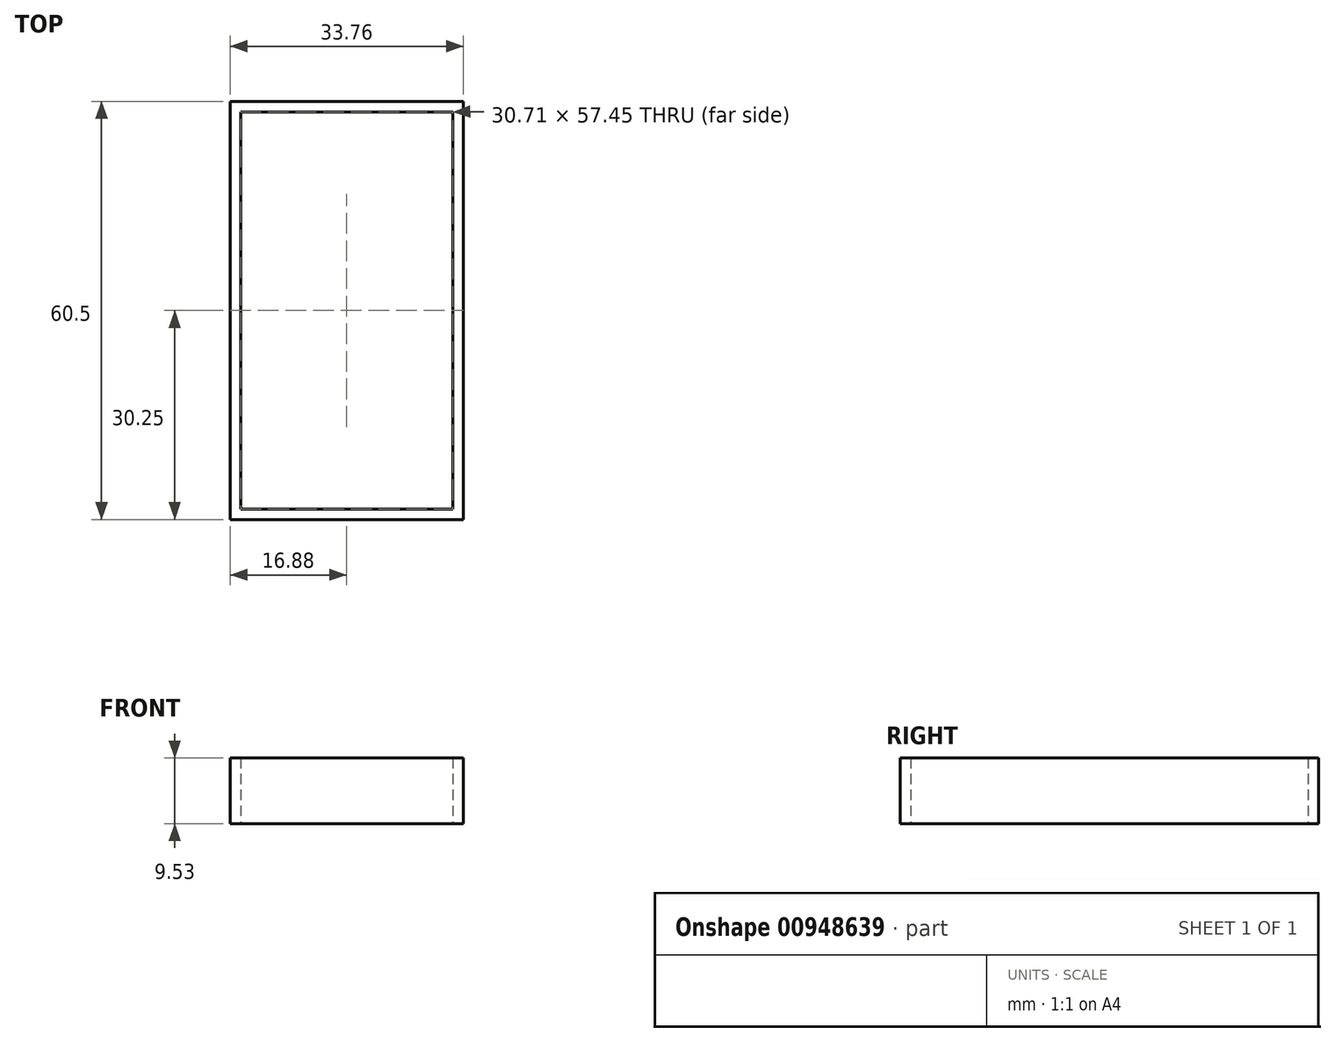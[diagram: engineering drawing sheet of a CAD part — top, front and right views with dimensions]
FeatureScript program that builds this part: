
annotation { "Feature Type Name" : "Feature", "Feature Type Description" : "" }
export const myFeature = defineFeature(function(context is Context, id is Id, definition is map)
    precondition{}
    {
        {
            var Q0;
            Q0=qCreatedBy(makeId("Top.planeOp"),FACE);
            var sketch = newSketch(context, id + "F0", { "sketchPlane" : qUnion([Q0])});
            skLineSegment(sketch, "E0.bottom", {"start": v(-15.35, 28.73) * mm, "end": v(15.35, 28.73) * mm});
            skLineSegment(sketch, "E0.top", {"start": v(-15.35, -28.73) * mm, "end": v(15.35, -28.73) * mm});
            skLineSegment(sketch, "E0.left", {"start": v(-15.35, 28.73) * mm, "end": v(-15.35, -28.73) * mm});
            skLineSegment(sketch, "E0.right", {"start": v(15.35, 28.73) * mm, "end": v(15.35, -28.73) * mm});
            skPoint(sketch, "E0.middle", {"position": v(0, 0) * mm});
            skLineSegment(sketch, "E1.bottom", {"start": v(-16.88, 30.25) * mm, "end": v(16.88, 30.25) * mm});
            skLineSegment(sketch, "E1.top", {"start": v(-16.88, -30.25) * mm, "end": v(16.88, -30.25) * mm});
            skLineSegment(sketch, "E1.left", {"start": v(-16.88, 30.25) * mm, "end": v(-16.88, -30.25) * mm});
            skLineSegment(sketch, "E1.right", {"start": v(16.88, 30.25) * mm, "end": v(16.88, -30.25) * mm});
            skSolve(sketch);
        }
        {
            var Q0;
            Q0=makeQuery(id+"F0.imprint","IMPRINT",FACE,{"disambiguationData":[TD([[makeQuery(id+"F0.imprint","IMPRINT",EDGE,{"derivedFrom":sQuery(id+"F0.wireOp",EDGE,"E0.bottom")}),1.0]])]});
            extrude(context, id + "F1", {"entities" : qUnion([Q0]), "depth" : 9.53 * mm, "offsetDistance" : 25.4 * mm});
        }
    });
